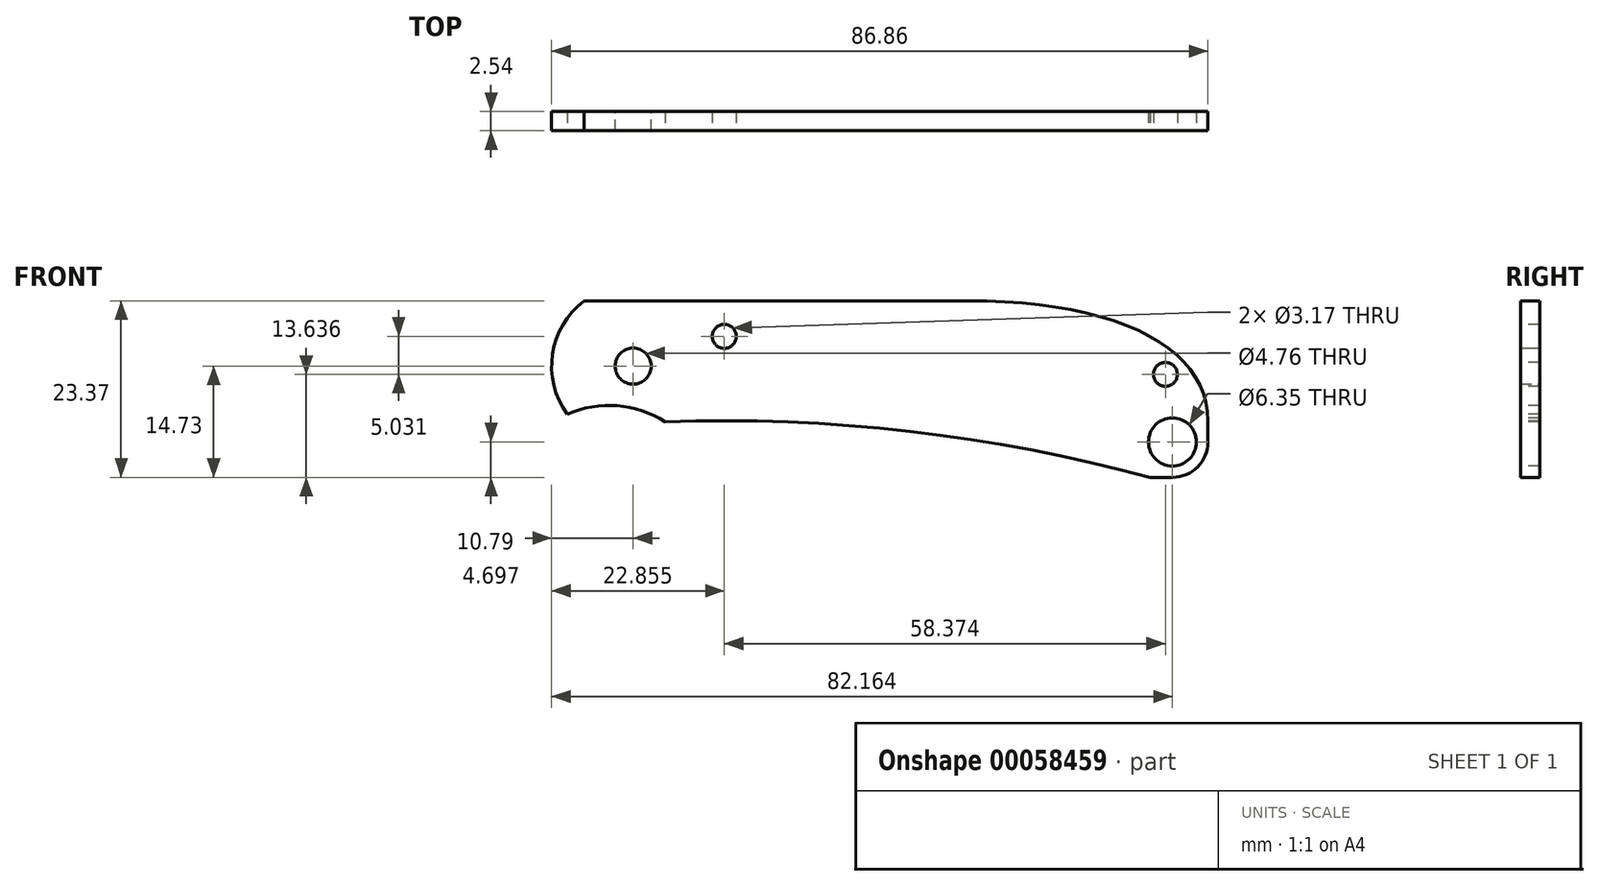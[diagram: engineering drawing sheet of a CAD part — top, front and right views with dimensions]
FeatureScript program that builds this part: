
annotation { "Feature Type Name" : "Feature", "Feature Type Description" : "" }
export const myFeature = defineFeature(function(context is Context, id is Id, definition is map)
    precondition{}
    {
        {
            var Q0;
            Q0=qCreatedBy(makeId("Front.planeOp"),FACE);
            var sketch = newSketch(context, id + "F0", { "sketchPlane" : qUnion([Q0])});
            skLineSegment(sketch, "E0.bottom", {"start": v(-6.48, -14.73) * mm, "end": v(76.07, -14.73) * mm});
            skLineSegment(sketch, "E0.top", {"start": v(-6.48, 8.64) * mm, "end": v(76.07, 8.64) * mm});
            skLineSegment(sketch, "E0.left", {"start": v(-6.48, -14.73) * mm, "end": v(-6.48, 8.64) * mm});
            skLineSegment(sketch, "E0.right", {"start": v(76.07, -14.73) * mm, "end": v(76.07, 8.64) * mm});
            skCircle(sketch, "E1", {"center": v(0, 0) * mm, "radius": 2.38 * mm});
            skSolve(sketch);
        }
        {
            var Q0;
            Q0 = qSketchRegion(id + "F0", true);
            extrude(context, id + "F1", {"entities" : qUnion([Q0]), "depth" : 2.54 * mm});
        }
        {
            var Q0;
            Q0=makeQuery(id+"F1.opExtrude","CAP_FACE",FACE,{"disambiguationData":[OSD([sQuery(id+"F0.wireOp",EDGE,"E0.bottom"),sQuery(id+"F0.wireOp",EDGE,"E0.top"),sQuery(id+"F0.wireOp",EDGE,"E0.left"),sQuery(id+"F0.wireOp",EDGE,"E0.right"),sQuery(id+"F0.wireOp",EDGE,"E1")])],"isStart":false});
            var sketch = newSketch(context, id + "F2", { "sketchPlane" : qUnion([Q0])});
            skCircle(sketch, "E2", {"center": v(12.07, 3.94) * mm, "radius": 1.59 * mm});
            skLineSegment(sketch, "E3", {"start": v(0, 0) * mm, "end": v(12.07, 3.94) * mm, "construction": true});
            skSolve(sketch);
        }
        {
            var Q0;
            Q0 = qSketchRegion(id + "F2", true);
            extrude(context, id + "F3", {"entities" : qUnion([Q0]), "operationType" : NewBodyOperationType.REMOVE, "endBound" : BoundingType.SYMMETRIC, "oppositeDirection" : true, "depth" : 25.4 * mm});
        }
        {
            var Q0;
            Q0=makeQuery(id+"F1.opExtrude","CAP_FACE",FACE,{"disambiguationData":[OSD([sQuery(id+"F0.wireOp",EDGE,"E0.bottom"),sQuery(id+"F0.wireOp",EDGE,"E0.top"),sQuery(id+"F0.wireOp",EDGE,"E0.left"),sQuery(id+"F0.wireOp",EDGE,"E0.right"),sQuery(id+"F0.wireOp",EDGE,"E1")])],"isStart":false});
            var sketch = newSketch(context, id + "F4", { "sketchPlane" : qUnion([Q0])});
            skArc(sketch, "E4", {"start": v(12.07, -7.24) * mm, "mid": v(2.79, -7.44) * mm, "end": v(-6.48, -8.04) * mm});
            skArc(sketch, "E5", {"start": v(68.45, -14.73) * mm, "mid": v(40.5, -9.12) * mm, "end": v(12.07, -7.24) * mm});
            skLineSegment(sketch, "E6", {"start": v(-6.48, -8.04) * mm, "end": v(-6.48, -14.73) * mm});
            skLineSegment(sketch, "E7", {"start": v(-6.48, -14.73) * mm, "end": v(68.45, -14.73) * mm});
            skEllipticalArc(sketch, "E8.trimOffspring", {});
            skLineSegment(sketch, "E9", {"start": v(76.07, 8.64) * mm, "end": v(76.07, -7.24) * mm});
            skLineSegment(sketch, "E10", {"start": v(44.32, 8.64) * mm, "end": v(76.07, 8.64) * mm});
            const initialGuessF4  = {"E8.trimOffspring": [0.013094713851788483, -0.02285314307410575, 0.9576456612362014, 0.28794927941475845, 0.06528356068928182, 0.026379677053299275, 6.1622777963541635, 0.9310662586939866]};
            skSetInitialGuess(sketch, initialGuessF4);
            skSolve(sketch);
        }
        {
            var Q0;
            Q0 = qSketchRegion(id + "F4", true);
            extrude(context, id + "F5", {"entities" : qUnion([Q0]), "operationType" : NewBodyOperationType.REMOVE, "endBound" : BoundingType.THROUGH_ALL, "oppositeDirection" : true, "depth" : 25.4 * mm});
        }
        {
            var Q0;
            Q0=makeQuery(id+"F1.opExtrude","CAP_FACE",FACE,{"disambiguationData":[OSD([sQuery(id+"F0.wireOp",EDGE,"E0.bottom"),sQuery(id+"F0.wireOp",EDGE,"E0.top"),sQuery(id+"F0.wireOp",EDGE,"E0.left"),sQuery(id+"F0.wireOp",EDGE,"E0.right"),sQuery(id+"F0.wireOp",EDGE,"E1")])],"isStart":false});
            var sketch = newSketch(context, id + "F6", { "sketchPlane" : qUnion([Q0])});
            skArc(sketch, "E11", {"start": v(6.35, -9.02) * mm, "mid": v(-3.17, -5.2) * mm, "end": v(-12.7, -9.02) * mm});
            skLineSegment(sketch, "E12", {"start": v(-12.7, -9.02) * mm, "end": v(6.35, -9.02) * mm});
            skSolve(sketch);
        }
        {
            var Q0;
            Q0 = qSketchRegion(id + "F6", true);
            extrude(context, id + "F7", {"entities" : qUnion([Q0]), "operationType" : NewBodyOperationType.REMOVE, "endBound" : BoundingType.THROUGH_ALL, "oppositeDirection" : true, "depth" : 25.4 * mm});
        }
        {
            var Q0;
            Q0=makeQuery(id+"F1.opExtrude","SWEPT_EDGE",EDGE,{"disambiguationData":[OSD([sQuery(id+"F0.wireOp",EDGE,"E0.bottom"),sQuery(id+"F0.wireOp",EDGE,"E0.right")])]});
            fillet(context, id + "F8", {"entities" : qUnion([Q0]), "radius" : 4.7 * mm, "tangentPropagation" : true, "allowEdgeOverflow" : false});
        }
        {
            var Q0;
            Q0=makeQuery(id+"F1.opExtrude","CAP_FACE",FACE,{"disambiguationData":[OSD([sQuery(id+"F0.wireOp",EDGE,"E0.bottom"),sQuery(id+"F0.wireOp",EDGE,"E0.top"),sQuery(id+"F0.wireOp",EDGE,"E0.left"),sQuery(id+"F0.wireOp",EDGE,"E0.right"),sQuery(id+"F0.wireOp",EDGE,"E1")])],"isStart":false});
            var sketch = newSketch(context, id + "F9", { "sketchPlane" : qUnion([Q0])});
            skArc(sketch, "E13", {"start": v(-6.48, 8.64) * mm, "mid": v(-10.68, 1.6) * mm, "end": v(-8.72, -6.37) * mm});
            skArc(sketch, "E14", {"start": v(-6.48, -5.6) * mm, "mid": v(-7.61, -5.94) * mm, "end": v(-8.72, -6.37) * mm});
            skLineSegment(sketch, "E15", {"start": v(-6.48, 8.64) * mm, "end": v(-6.48, -5.6) * mm});
            skSolve(sketch);
        }
        {
            var Q0;
            Q0 = qSketchRegion(id + "F9", true);
            extrude(context, id + "F10", {"entities" : qUnion([Q0]), "operationType" : NewBodyOperationType.ADD, "oppositeDirection" : true, "depth" : 2.54 * mm});
        }
        {
            var Q0;
            Q0=makeQuery(id+"F10.boolean.opBoolean","MERGE",FACE,{"derivedFrom":[makeQuery(id+"F1.opExtrude","CAP_FACE",FACE,{"disambiguationData":[OSD([sQuery(id+"F0.wireOp",EDGE,"E0.bottom"),sQuery(id+"F0.wireOp",EDGE,"E0.top"),sQuery(id+"F0.wireOp",EDGE,"E0.left"),sQuery(id+"F0.wireOp",EDGE,"E0.right"),sQuery(id+"F0.wireOp",EDGE,"E1")])],"isStart":false}),makeQuery(id+"F10.opExtrude","CAP_FACE",FACE,{"disambiguationData":[OSD([sQuery(id+"F9.wireOp",EDGE,"E13"),sQuery(id+"F9.wireOp",EDGE,"E14"),sQuery(id+"F9.wireOp",EDGE,"E15")])],"isStart":true})]});
            var sketch = newSketch(context, id + "F11", { "sketchPlane" : qUnion([Q0])});
            skCircle(sketch, "E16", {"center": v(0, 0) * mm, "radius": 68.64 * mm, "construction": true});
            skCircle(sketch, "E17", {"center": v(71.37, -10.03) * mm, "radius": 3.18 * mm});
            skCircle(sketch, "E18", {"center": v(70.44, -1.1) * mm, "radius": 1.59 * mm});
            skSolve(sketch);
        }
        {
            var Q0;
            Q0 = qSketchRegion(id + "F11", true);
            extrude(context, id + "F12", {"entities" : qUnion([Q0]), "operationType" : NewBodyOperationType.REMOVE, "endBound" : BoundingType.THROUGH_ALL, "oppositeDirection" : true, "depth" : 25.4 * mm});
        }
    });
